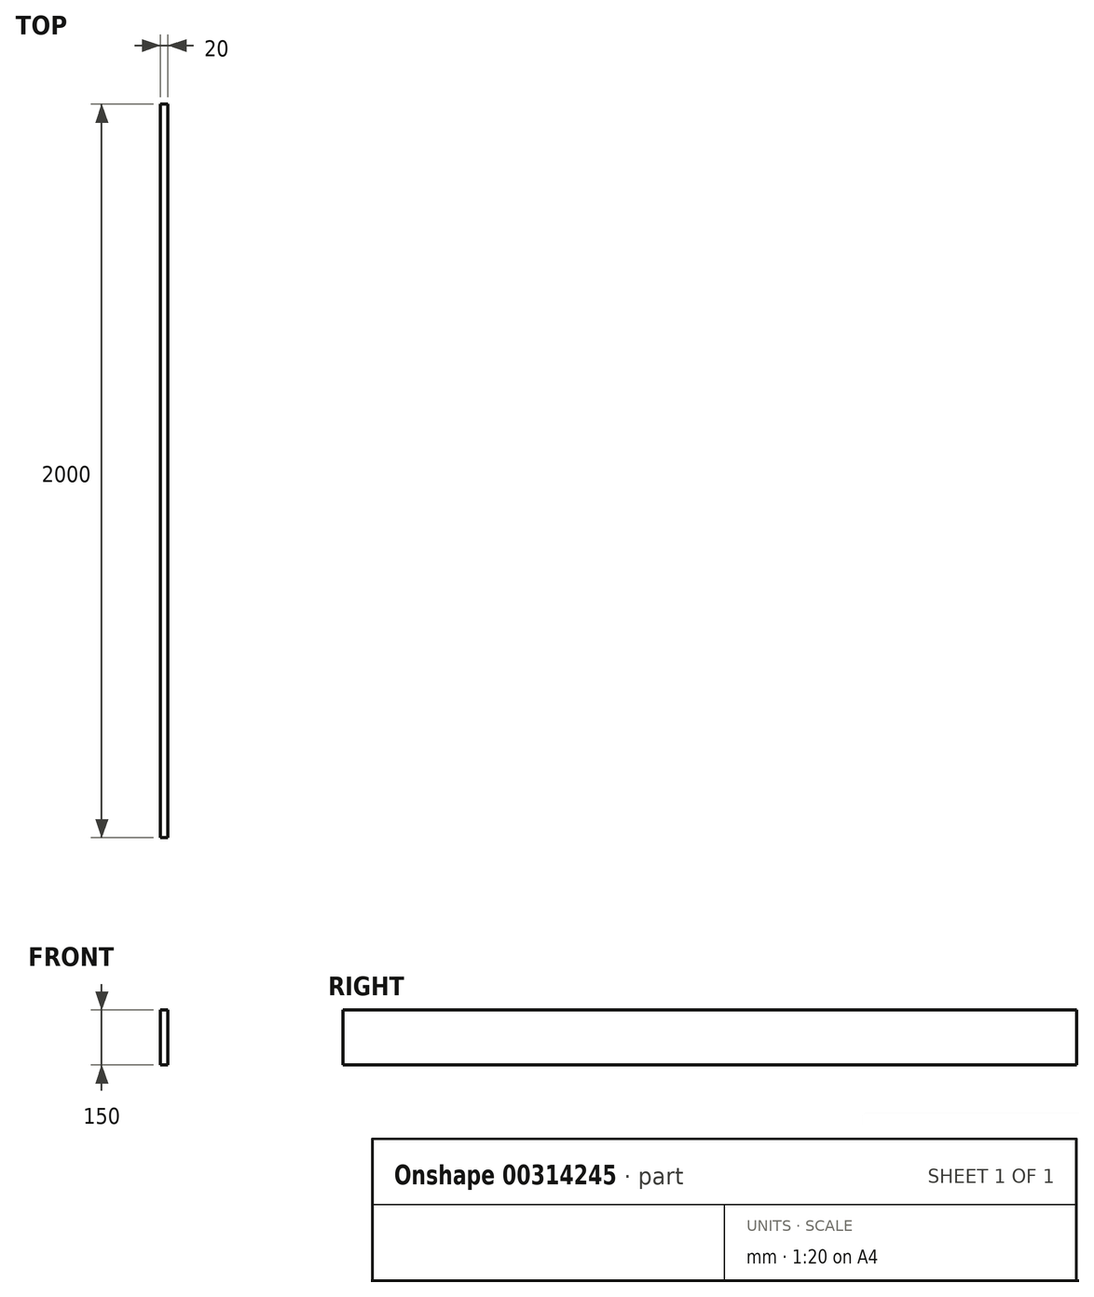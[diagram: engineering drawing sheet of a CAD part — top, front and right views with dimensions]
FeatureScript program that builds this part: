
annotation { "Feature Type Name" : "Feature", "Feature Type Description" : "" }
export const myFeature = defineFeature(function(context is Context, id is Id, definition is map)
    precondition{}
    {
        {
            assignVariable(context, id + "F0", {"name" : "Lg", "anyValue" : 2000});
        }
        {
            var Q0;
            Q0=qCreatedBy(makeId("Front.planeOp"),FACE);
            var sketch = newSketch(context, id + "F1", { "sketchPlane" : qUnion([Q0])});
            skLineSegment(sketch, "E0.bottom", {"start": v(0, 0) * mm, "end": v(20, 0) * mm});
            skLineSegment(sketch, "E0.top", {"start": v(0, 150) * mm, "end": v(20, 150) * mm});
            skLineSegment(sketch, "E0.left", {"start": v(0, 0) * mm, "end": v(0, 150) * mm});
            skLineSegment(sketch, "E0.right", {"start": v(20, 0) * mm, "end": v(20, 150) * mm});
            skSolve(sketch);
        }
        {
            var Q0;
            Q0 = qSketchRegion(id + "F1", true);
            var Q1;
            Q1=makeQuery(id+"F1.imprint","IMPRINT",FACE,{"disambiguationData":[TD([[makeQuery(id+"F1.imprint","IMPRINT",EDGE,{"derivedFrom":sQuery(id+"F1.wireOp",EDGE,"E0.bottom")}),1.0]])]});
            extrude(context, id + "F2", {"entities" : qUnion([Q0, Q1]), "depth" : getVariable(context, 'Lg') * mm});
        }
    });
